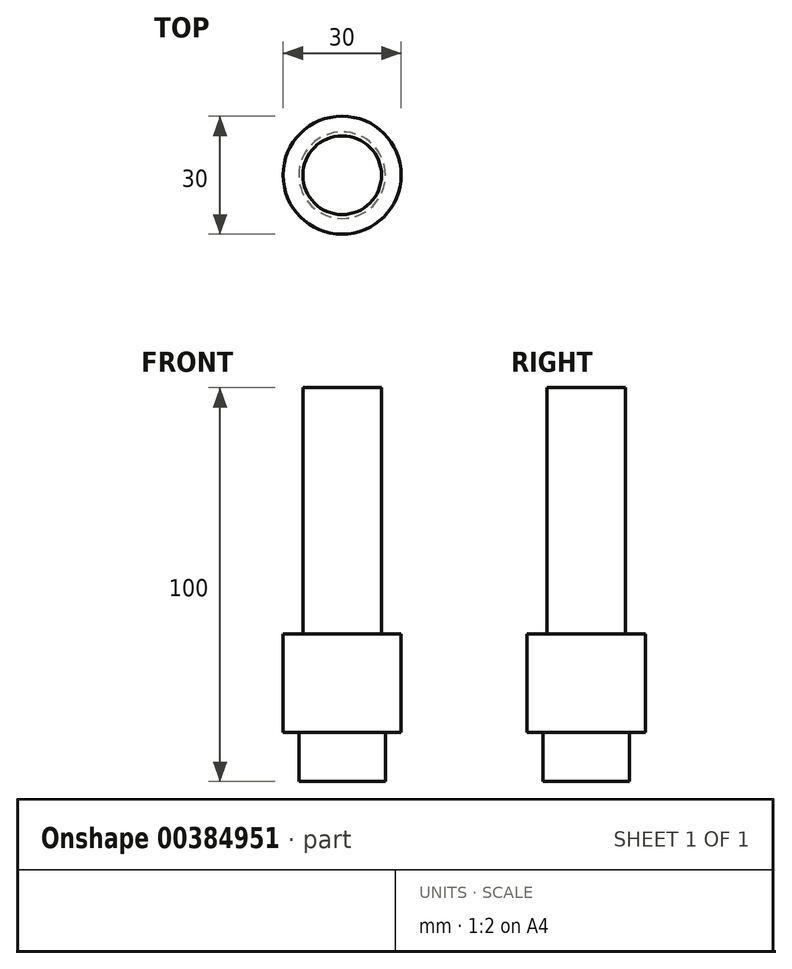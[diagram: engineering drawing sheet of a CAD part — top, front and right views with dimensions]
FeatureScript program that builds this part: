
annotation { "Feature Type Name" : "Feature", "Feature Type Description" : "" }
export const myFeature = defineFeature(function(context is Context, id is Id, definition is map)
    precondition{}
    {
        {
            var Q0;
            Q0=qCreatedBy(makeId("Front.planeOp"),FACE);
            var sketch = newSketch(context, id + "F0", { "sketchPlane" : qUnion([Q0])});
            skLineSegment(sketch, "E0", {"start": v(0, 70.17) * mm, "end": v(0, -61.2) * mm, "construction": true});
            skLineSegment(sketch, "E1", {"start": v(0, 70.17) * mm, "end": v(-10, 70.17) * mm});
            skLineSegment(sketch, "E2", {"start": v(-10, 70.17) * mm, "end": v(-10, 7.59) * mm});
            skLineSegment(sketch, "E3", {"start": v(-10, 7.59) * mm, "end": v(-15, 7.59) * mm});
            skLineSegment(sketch, "E4", {"start": v(-15, 7.59) * mm, "end": v(-15, -17.41) * mm});
            skLineSegment(sketch, "E5", {"start": v(-15, -17.41) * mm, "end": v(-11, -17.41) * mm});
            skLineSegment(sketch, "E6", {"start": v(-11, -17.41) * mm, "end": v(-11, -29.83) * mm});
            skLineSegment(sketch, "E7", {"start": v(-11, -29.83) * mm, "end": v(0, -29.83) * mm});
            skLineSegment(sketch, "E8", {"start": v(0, -29.83) * mm, "end": v(0, 70.17) * mm});
            skSolve(sketch);
        }
        {
            var Q0;
            Q0 = qSketchRegion(id + "F0", true);
            var Q1;
            Q1=sQuery(id+"F0.wireOp",EDGE,"E0");
            revolve(context, id + "F1", {"entities" : qUnion([Q0]), "axis" : qUnion([Q1]), "revolveType" : RevolveType.FULL});
        }
    });
